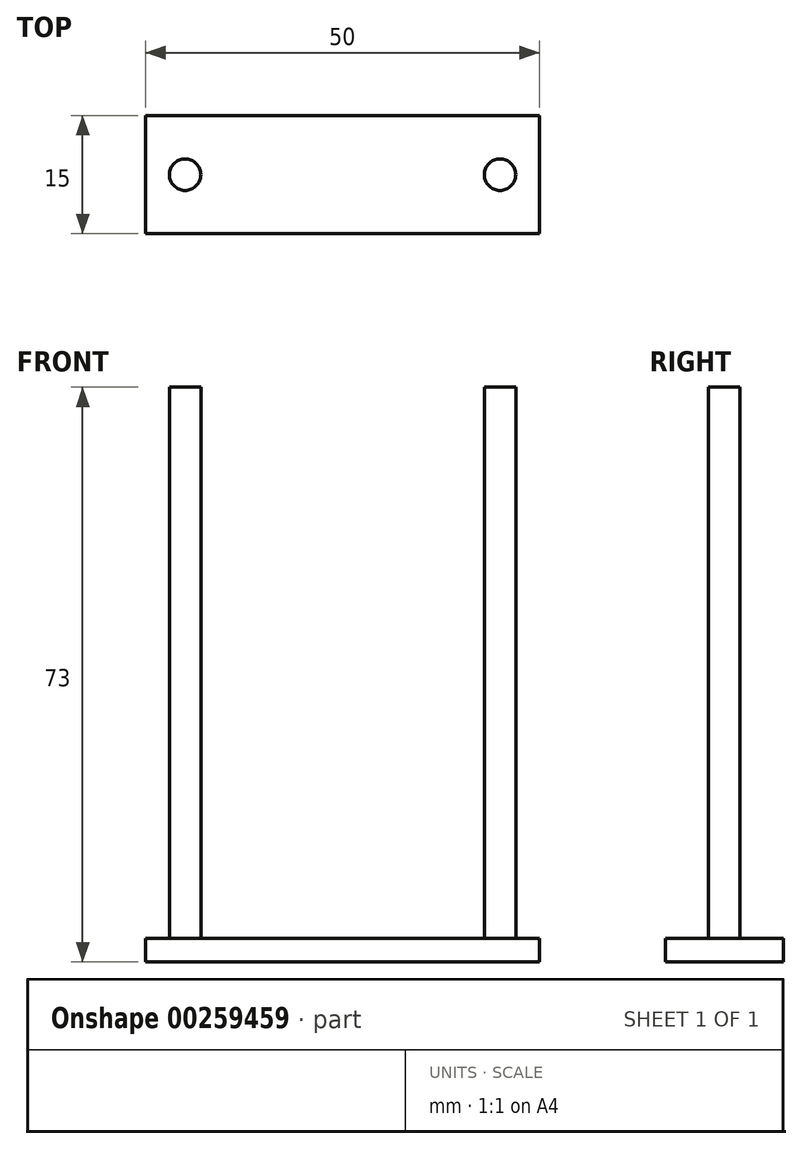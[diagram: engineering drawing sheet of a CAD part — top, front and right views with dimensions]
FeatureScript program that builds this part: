
annotation { "Feature Type Name" : "Feature", "Feature Type Description" : "" }
export const myFeature = defineFeature(function(context is Context, id is Id, definition is map)
    precondition{}
    {
        {
            var Q0;
            Q0=qCreatedBy(makeId("Top.planeOp"),FACE);
            var sketch = newSketch(context, id + "F0", { "sketchPlane" : qUnion([Q0])});
            skLineSegment(sketch, "E0.bottom", {"start": v(-25, 7.5) * mm, "end": v(25, 7.5) * mm});
            skLineSegment(sketch, "E0.top", {"start": v(-25, -7.5) * mm, "end": v(25, -7.5) * mm});
            skLineSegment(sketch, "E0.left", {"start": v(-25, 7.5) * mm, "end": v(-25, -7.5) * mm});
            skLineSegment(sketch, "E0.right", {"start": v(25, 7.5) * mm, "end": v(25, -7.5) * mm});
            skSolve(sketch);
        }
        {
            var Q0;
            Q0=makeQuery(id+"F0.imprint","IMPRINT",FACE,{"disambiguationData":[TD([[makeQuery(id+"F0.imprint","IMPRINT",EDGE,{"derivedFrom":sQuery(id+"F0.wireOp",EDGE,"E0.bottom")}),-1.0]])]});
            extrude(context, id + "F1", {"entities" : qUnion([Q0]), "depth" : 3 * mm});
        }
        {
            var Q0;
            Q0=makeQuery(id+"F1.opExtrude","CAP_FACE",FACE,{"disambiguationData":[OSD([sQuery(id+"F0.wireOp",EDGE,"E0.bottom"),sQuery(id+"F0.wireOp",EDGE,"E0.top"),sQuery(id+"F0.wireOp",EDGE,"E0.left"),sQuery(id+"F0.wireOp",EDGE,"E0.right")])],"isStart":false});
            var sketch = newSketch(context, id + "F2", { "sketchPlane" : qUnion([Q0])});
            skCircle(sketch, "E1", {"center": v(-20, 0) * mm, "radius": 2 * mm});
            skSolve(sketch);
        }
        {
            var Q0;
            Q0 = qSketchRegion(id + "F2", true);
            var Q1;
            Q1=sQuery(id+"F2.wireOp",EDGE,"E1");
            extrude(context, id + "F3", {"entities" : qUnion([Q0]), "surfaceEntities" : qUnion([Q1]), "depth" : 70 * mm});
        }
        {
            var Q0;
            Q0=makeQuery(id+"F3.opExtrude","SWEPT_BODY",BODY,{"disambiguationData":[OSD([sQuery(id+"F2.wireOp",EDGE,"E1")])]});
            var Q1;
            Q1=qCreatedBy(makeId("Right.planeOp"),FACE);
            mirror(context, id + "F4", {"entities" : qUnion([Q0]), "mirrorPlane" : qUnion([Q1])});
        }
    });
